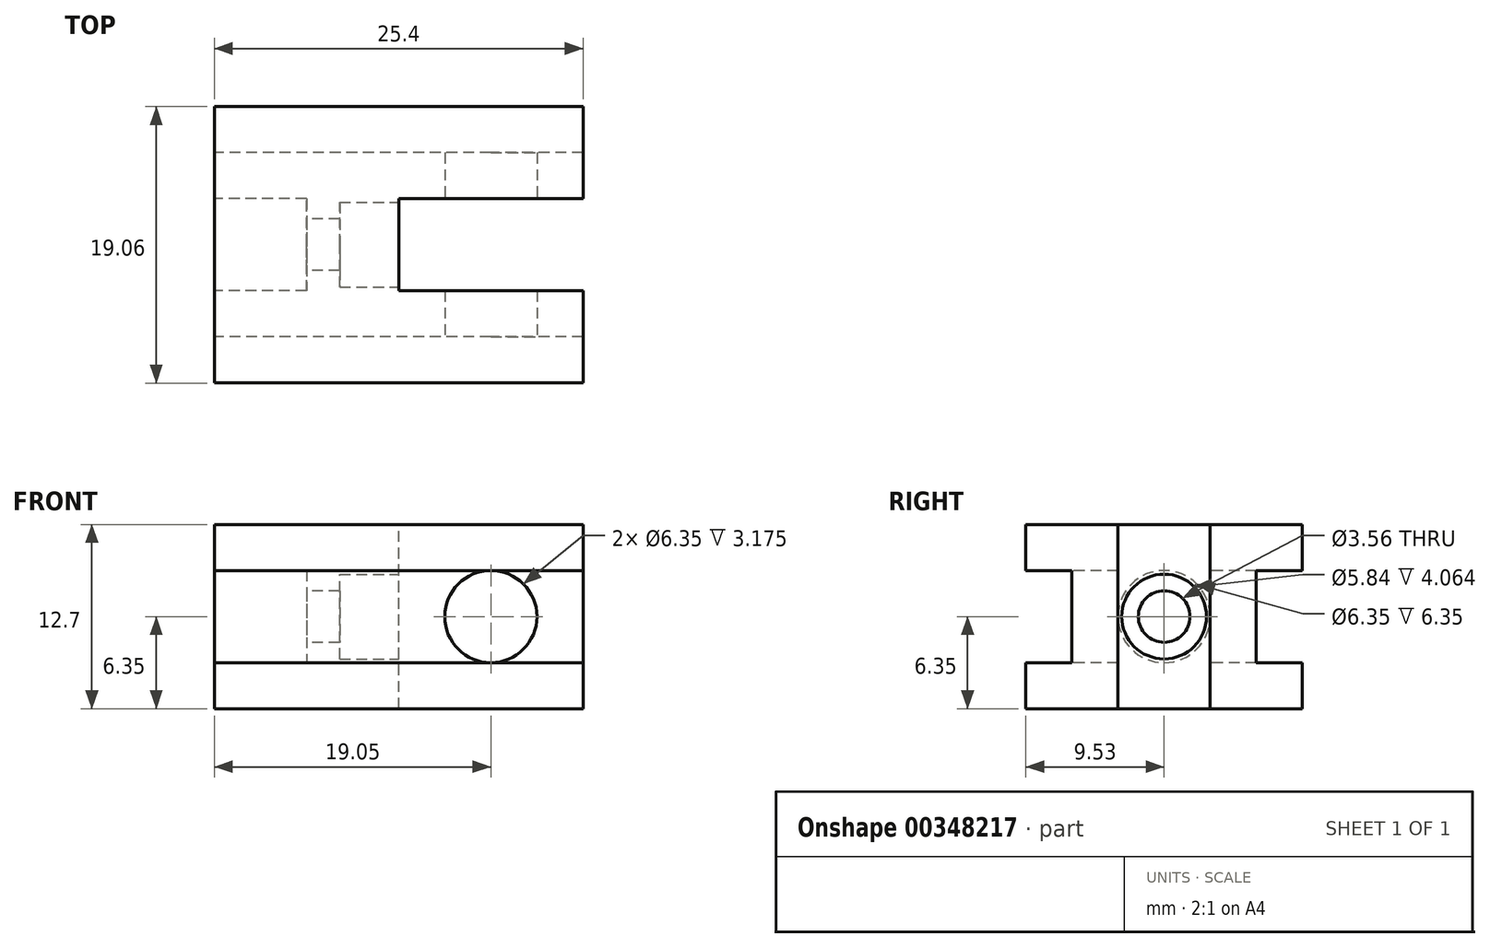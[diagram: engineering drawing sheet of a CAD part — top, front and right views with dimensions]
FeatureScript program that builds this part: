
annotation { "Feature Type Name" : "Feature", "Feature Type Description" : "" }
export const myFeature = defineFeature(function(context is Context, id is Id, definition is map)
    precondition{}
    {
        {
            var Q0;
            Q0=qCreatedBy(makeId("Right.planeOp"),FACE);
            var sketch = newSketch(context, id + "F0", { "sketchPlane" : qUnion([Q0])});
            skLineSegment(sketch, "E0", {"start": v(-6.35, -3.17) * mm, "end": v(-6.35, 3.17) * mm});
            skLineSegment(sketch, "E1", {"start": v(-6.35, 3.17) * mm, "end": v(-9.53, 3.17) * mm});
            skLineSegment(sketch, "E2", {"start": v(-9.52, 3.17) * mm, "end": v(-9.52, 6.35) * mm});
            skLineSegment(sketch, "E3", {"start": v(-9.52, 6.35) * mm, "end": v(9.52, 6.35) * mm});
            skLineSegment(sketch, "E4", {"start": v(9.53, 6.35) * mm, "end": v(9.53, 3.17) * mm});
            skLineSegment(sketch, "E5", {"start": v(9.53, 3.17) * mm, "end": v(6.35, 3.17) * mm});
            skLineSegment(sketch, "E6", {"start": v(6.35, 3.17) * mm, "end": v(6.35, -3.17) * mm});
            skLineSegment(sketch, "E7", {"start": v(6.35, -3.17) * mm, "end": v(9.53, -3.17) * mm});
            skLineSegment(sketch, "E8", {"start": v(9.52, -3.17) * mm, "end": v(9.52, -6.35) * mm});
            skLineSegment(sketch, "E9", {"start": v(9.53, -6.35) * mm, "end": v(-9.53, -6.35) * mm});
            skLineSegment(sketch, "E10", {"start": v(-9.53, -6.35) * mm, "end": v(-9.53, -3.17) * mm});
            skLineSegment(sketch, "E11", {"start": v(-9.53, -3.17) * mm, "end": v(-6.35, -3.17) * mm});
            skPoint(sketch, "E12", {"position": v(0, 6.35) * mm});
            skPoint(sketch, "E13", {"position": v(6.35, 0) * mm});
            skCircle(sketch, "E14", {"center": v(0, 0) * mm, "radius": 1.78 * mm});
            skSolve(sketch);
        }
        {
            var Q0;
            Q0=qSketchRegion(id+"F0",true);
            extrude(context, id + "F1", {"entities" : qUnion([Q0]), "endBound" : BoundingType.SYMMETRIC, "depth" : 25.4 * mm});
        }
        {
            var Q0;
            Q0=qCreatedBy(makeId("Front.planeOp"),FACE);
            var sketch = newSketch(context, id + "F2", { "sketchPlane" : qUnion([Q0])});
            skCircle(sketch, "E15", {"center": v(6.35, 0) * mm, "radius": 3.18 * mm});
            skSolve(sketch);
        }
        {
            var Q0;
            Q0=qSketchRegion(id+"F2",true);
            extrude(context, id + "F3", {"entities" : qUnion([Q0]), "operationType" : NewBodyOperationType.REMOVE, "endBound" : BoundingType.SYMMETRIC, "oppositeDirection" : true, "depth" : 25.4 * mm});
        }
        {
            var Q0;
            Q0=qCreatedBy(makeId("Top.planeOp"),FACE);
            var sketch = newSketch(context, id + "F4", { "sketchPlane" : qUnion([Q0])});
            skLineSegment(sketch, "E16.bottom", {"start": v(12.7, -3.18) * mm, "end": v(0, -3.18) * mm});
            skLineSegment(sketch, "E16.top", {"start": v(12.7, 3.18) * mm, "end": v(0, 3.18) * mm});
            skLineSegment(sketch, "E16.left", {"start": v(12.7, -3.18) * mm, "end": v(12.7, 3.18) * mm});
            skLineSegment(sketch, "E16.right", {"start": v(0, -3.18) * mm, "end": v(0, 3.18) * mm});
            skPoint(sketch, "E17", {"position": v(0, 0) * mm});
            skSolve(sketch);
        }
        {
            var Q0;
            Q0=qSketchRegion(id+"F4",true);
            extrude(context, id + "F5", {"entities" : qUnion([Q0]), "operationType" : NewBodyOperationType.REMOVE, "endBound" : BoundingType.SYMMETRIC, "oppositeDirection" : true, "depth" : 25.4 * mm});
        }
        {
            var Q0;
            Q0=makeQuery(id+"F5.boolean.opBoolean","COPY",FACE,{"derivedFrom":makeQuery(id+"F5.opExtrude","SWEPT_FACE",FACE,{"disambiguationData":[OSD([sQuery(id+"F4.wireOp",EDGE,"E16.right")])]})});
            var sketch = newSketch(context, id + "F6", { "sketchPlane" : qUnion([Q0])});
            skCircle(sketch, "E18", {"center": v(0, 0) * mm, "radius": 2.92 * mm});
            skSolve(sketch);
        }
        {
            var Q0;
            Q0=qSketchRegion(id+"F6",true);
            extrude(context, id + "F7", {"entities" : qUnion([Q0]), "operationType" : NewBodyOperationType.REMOVE, "oppositeDirection" : true, "depth" : 4.06 * mm});
        }
        {
            var Q0;
            Q0=makeQuery(id+"F1.opExtrude","CAP_FACE",FACE,{"disambiguationData":[OSD([sQuery(id+"F0.wireOp",EDGE,"E0"),sQuery(id+"F0.wireOp",EDGE,"E1"),sQuery(id+"F0.wireOp",EDGE,"E2"),sQuery(id+"F0.wireOp",EDGE,"E3"),sQuery(id+"F0.wireOp",EDGE,"E4"),sQuery(id+"F0.wireOp",EDGE,"E5"),sQuery(id+"F0.wireOp",EDGE,"E6"),sQuery(id+"F0.wireOp",EDGE,"E7"),sQuery(id+"F0.wireOp",EDGE,"E8"),sQuery(id+"F0.wireOp",EDGE,"E9"),sQuery(id+"F0.wireOp",EDGE,"E10"),sQuery(id+"F0.wireOp",EDGE,"E11"),sQuery(id+"F0.wireOp",EDGE,"E14")])],"isStart":true});
            var sketch = newSketch(context, id + "F8", { "sketchPlane" : qUnion([Q0])});
            skCircle(sketch, "E19", {"center": v(0, 0) * mm, "radius": 3.18 * mm});
            skSolve(sketch);
        }
        {
            var Q0;
            Q0=qSketchRegion(id+"F8",true);
            extrude(context, id + "F9", {"entities" : qUnion([Q0]), "operationType" : NewBodyOperationType.REMOVE, "oppositeDirection" : true, "depth" : 6.35 * mm});
        }
    });
